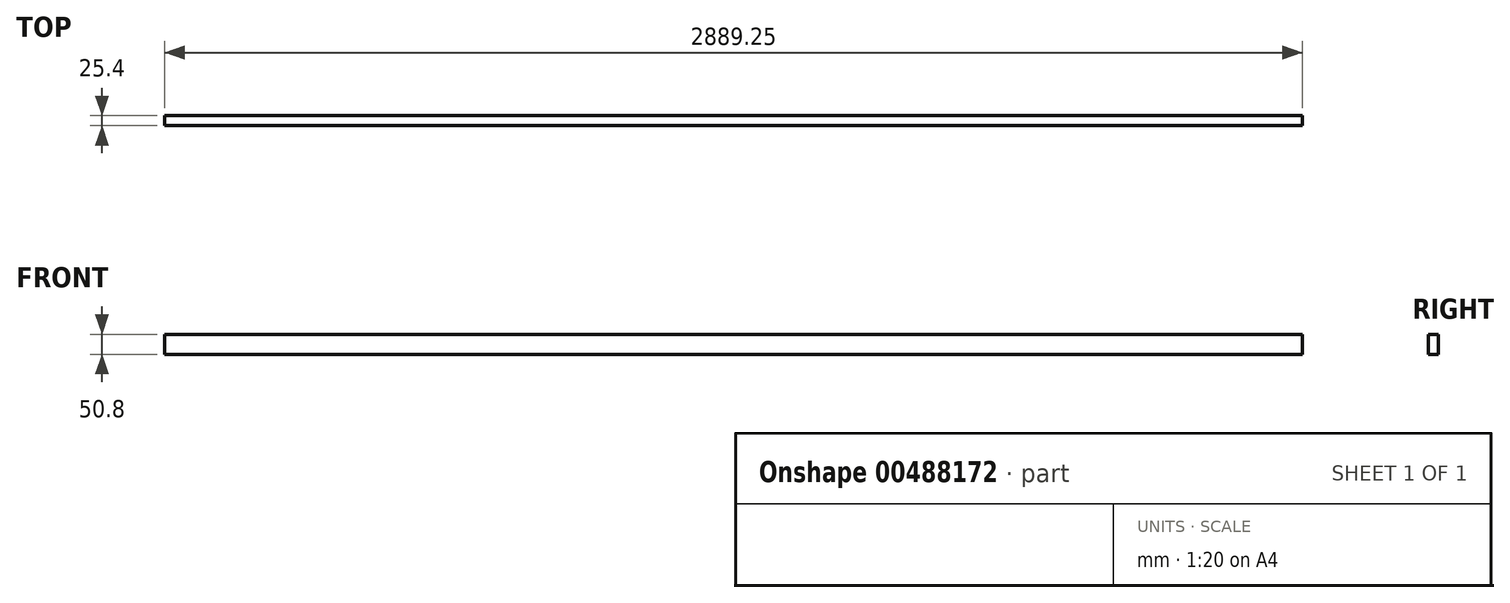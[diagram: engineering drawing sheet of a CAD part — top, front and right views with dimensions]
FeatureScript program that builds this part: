
annotation { "Feature Type Name" : "Feature", "Feature Type Description" : "" }
export const myFeature = defineFeature(function(context is Context, id is Id, definition is map)
    precondition{}
    {
        {
            var Q0;
            Q0=qCreatedBy(makeId("Front.planeOp"),FACE);
            var sketch = newSketch(context, id + "F0", { "sketchPlane" : qUnion([Q0])});
            skLineSegment(sketch, "E0", {"start": v(0, 0) * mm, "end": v(0, 50.8) * mm});
            skLineSegment(sketch, "E1", {"start": v(0, 50.8) * mm, "end": v(25.4, 50.8) * mm});
            skLineSegment(sketch, "E2", {"start": v(25.4, 50.8) * mm, "end": v(25.4, 0) * mm});
            skLineSegment(sketch, "E3", {"start": v(25.4, 0) * mm, "end": v(0, 0) * mm});
            skSolve(sketch);
        }
        {
            var Q0;
            Q0=makeQuery(id+"F0.imprint","IMPRINT",FACE,{"disambiguationData":[TD([[makeQuery(id+"F0.imprint","IMPRINT",EDGE,{"derivedFrom":sQuery(id+"F0.wireOp",EDGE,"E0")}),-1.0]])]});
            extrude(context, id + "F1", {"entities" : qUnion([Q0]), "depth" : 25.4 * mm, "offsetDistance" : 25.4 * mm});
        }
        {
            var Q0;
            Q0=makeQuery(id+"F1.opExtrude","SWEPT_FACE",FACE,{"disambiguationData":[OSD([sQuery(id+"F0.wireOp",EDGE,"E2")])]});
            extrude(context, id + "F2", {"entities" : qUnion([Q0]), "operationType" : NewBodyOperationType.ADD, "depth" : 2863.85 * mm, "offsetDistance" : 25.4 * mm});
        }
    });
